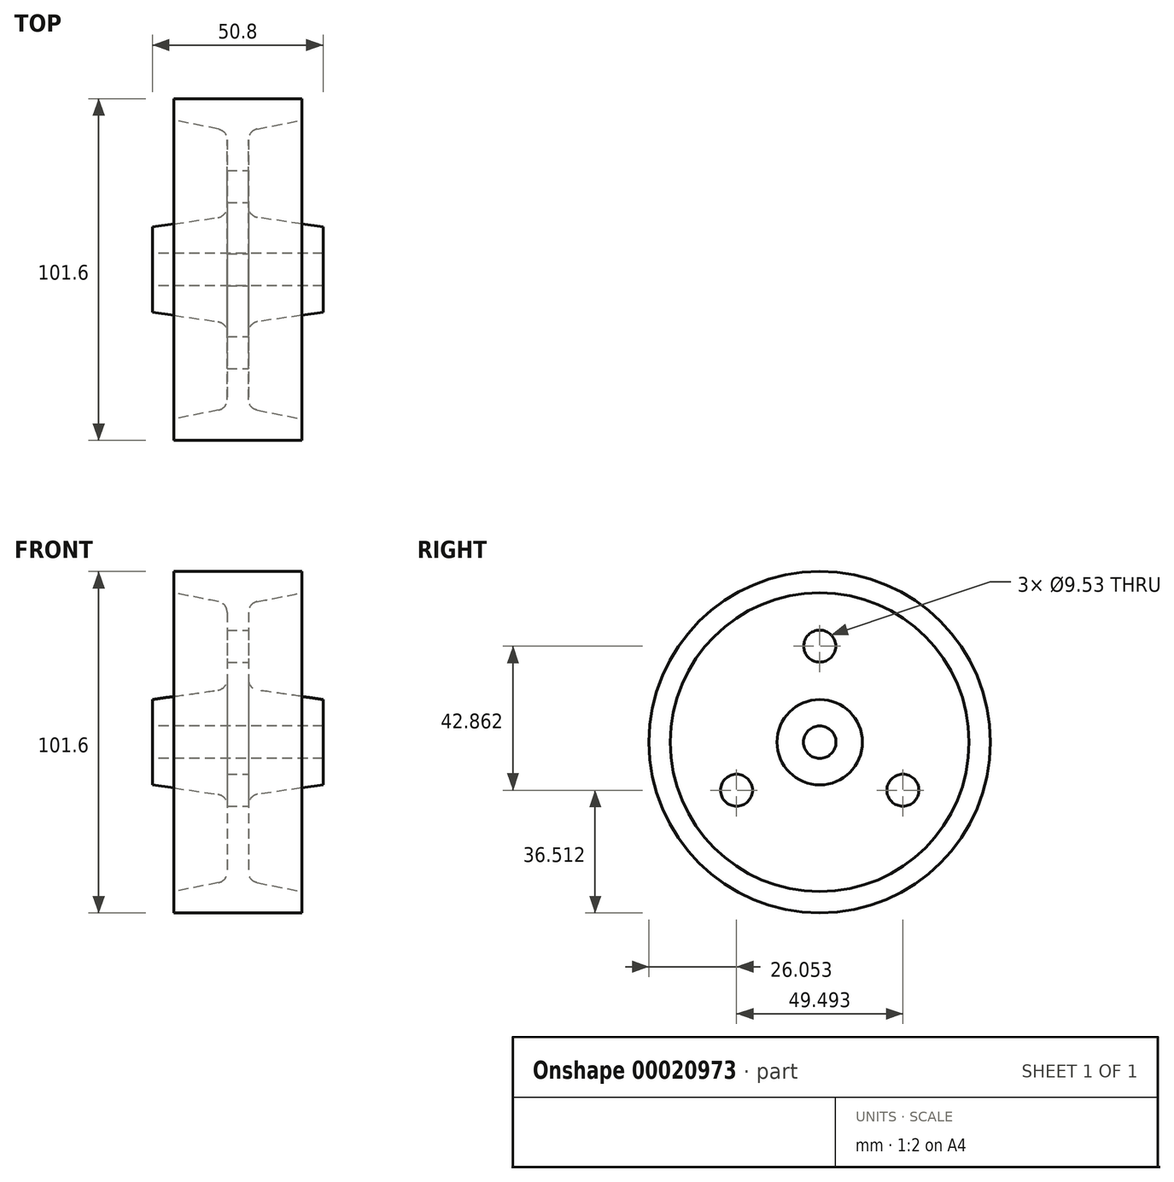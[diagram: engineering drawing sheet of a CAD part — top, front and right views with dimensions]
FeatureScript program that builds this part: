
annotation { "Feature Type Name" : "Feature", "Feature Type Description" : "" }
export const myFeature = defineFeature(function(context is Context, id is Id, definition is map)
    precondition{}
    {
        {
            var Q0;
            Q0=qCreatedBy(makeId("Front.planeOp"),FACE);
            var sketch = newSketch(context, id + "F0", { "sketchPlane" : qUnion([Q0])});
            skPoint(sketch, "E0", {"position": v(0, -4.83) * mm});
            skLineSegment(sketch, "E1", {"start": v(0, -4.83) * mm, "end": v(-25.4, -4.83) * mm});
            skLineSegment(sketch, "E2", {"start": v(0, -4.83) * mm, "end": v(25.4, -4.83) * mm});
            skLineSegment(sketch, "E3", {"start": v(-25.4, -4.83) * mm, "end": v(-25.4, -12.7) * mm});
            skLineSegment(sketch, "E4", {"start": v(25.4, -4.83) * mm, "end": v(25.4, -12.7) * mm});
            skLineSegment(sketch, "E5", {"start": v(-25.4, -12.7) * mm, "end": v(-5.9, -15.49) * mm});
            skLineSegment(sketch, "E6", {"start": v(25.4, -12.7) * mm, "end": v(5.9, -15.49) * mm});
            skLineSegment(sketch, "E7", {"start": v(-3.18, -18.63) * mm, "end": v(-3.18, -38.67) * mm});
            skLineSegment(sketch, "E8", {"start": v(3.18, -18.63) * mm, "end": v(3.18, -38.67) * mm});
            skLineSegment(sketch, "E9", {"start": v(-3.17, -50.8) * mm, "end": v(3.18, -50.8) * mm});
            skLineSegment(sketch, "E10", {"start": v(-3.18, -50.8) * mm, "end": v(-19.05, -50.8) * mm});
            skLineSegment(sketch, "E11", {"start": v(3.18, -50.8) * mm, "end": v(19.05, -50.8) * mm});
            skLineSegment(sketch, "E12", {"start": v(-19.05, -50.8) * mm, "end": v(-19.05, -44.45) * mm});
            skLineSegment(sketch, "E13", {"start": v(19.05, -44.45) * mm, "end": v(19.05, -50.8) * mm});
            skLineSegment(sketch, "E14", {"start": v(-19.05, -44.45) * mm, "end": v(-5.73, -41.79) * mm});
            skLineSegment(sketch, "E15", {"start": v(5.73, -41.79) * mm, "end": v(19.05, -44.45) * mm});
            skArc(sketch, "E16.filletArc", {"start": v(-3.17, -18.63) * mm, "mid": v(-3.95, -16.55) * mm, "end": v(-5.9, -15.49) * mm});
            skPoint(sketch, "E17.newPointB", {"position": v(3.18, 0) * mm});
            skArc(sketch, "E17.filletArc", {"start": v(5.9, -15.49) * mm, "mid": v(3.95, -16.55) * mm, "end": v(3.17, -18.63) * mm});
            skPoint(sketch, "E18.visualSharp", {"position": v(3.17, -41.28) * mm});
            skArc(sketch, "E18.filletArc", {"start": v(3.18, -38.67) * mm, "mid": v(3.9, -40.69) * mm, "end": v(5.73, -41.79) * mm});
            skPoint(sketch, "E19.visualSharp", {"position": v(-3.18, -41.28) * mm});
            skArc(sketch, "E19.filletArc", {"start": v(-5.73, -41.79) * mm, "mid": v(-3.9, -40.69) * mm, "end": v(-3.17, -38.67) * mm});
            skPoint(sketch, "E20.orphan", {"position": v(-3.18, -15.88) * mm});
            skPoint(sketch, "E21.end.orphan", {"position": v(3.18, -15.88) * mm});
            skPoint(sketch, "E22.orphan", {"position": v(-25.4, 0) * mm});
            skPoint(sketch, "E23.orphan", {"position": v(25.4, 0) * mm});
            skLineSegment(sketch, "E24", {"start": v(-25.4, 0) * mm, "end": v(25.4, 0) * mm});
            skSolve(sketch);
        }
        {
            var Q0;
            Q0=makeQuery(id+"F0.imprint","IMPRINT",FACE,{"disambiguationData":[TD([[makeQuery(id+"F0.imprint","IMPRINT",EDGE,{"derivedFrom":sQuery(id+"F0.wireOp",EDGE,"E1")}),1.0]])]});
            var Q1;
            Q1=sQuery(id+"F0.wireOp",EDGE,"E24");
            revolve(context, id + "F1", {"entities" : qUnion([Q0]), "axis" : qUnion([Q1]), "revolveType" : RevolveType.FULL});
        }
        {
            var Q0;
            Q0=qCreatedBy(makeId("Right.planeOp"),FACE);
            var sketch = newSketch(context, id + "F2", { "sketchPlane" : qUnion([Q0])});
            skCircle(sketch, "E25", {"center": v(0, 0) * mm, "radius": 28.57 * mm, "construction": true});
            skLineSegment(sketch, "E26", {"start": v(-24.75, -14.29) * mm, "end": v(0, 28.58) * mm, "construction": true});
            skLineSegment(sketch, "E27", {"start": v(0, 28.58) * mm, "end": v(24.75, -14.29) * mm, "construction": true});
            skLineSegment(sketch, "E28", {"start": v(24.75, -14.29) * mm, "end": v(-24.75, -14.29) * mm, "construction": true});
            skCircle(sketch, "E29", {"center": v(0, 28.58) * mm, "radius": 4.76 * mm});
            skCircle(sketch, "E30", {"center": v(-24.75, -14.29) * mm, "radius": 4.76 * mm});
            skCircle(sketch, "E31", {"center": v(24.75, -14.29) * mm, "radius": 4.76 * mm});
            skSolve(sketch);
        }
        {
            var Q0;
            Q0 = qSketchRegion(id + "F2", true);
            extrude(context, id + "F3", {"entities" : qUnion([Q0]), "operationType" : NewBodyOperationType.REMOVE, "endBound" : BoundingType.SYMMETRIC, "oppositeDirection" : true, "depth" : 72.64 * mm});
        }
    });
